# Revit family: 0053546 Feilo Sylvania Lighting Fixture START SPOT LED IP65 4000K G2
name_source: partatom
category: Lighting Fixtures
revit_build: Autodesk Revit 2017 (Build: 20190507_1515(x64)
units: mm (PartAtom-declared; Revit-internal decimal feet)

## family parameters
Cut with Voids When Loaded = No
Host = Face
Light Source = Yes
OmniClass Number = 23.80.70.00
OmniClass Title = Lighting
Part Type = Normal
Room Calculation Point = No
Round Connector Dimension = Use Diameter
Shared = No

## types (1)
- 0053546 START SPOT LED IP65 4000K G2
    Apparent Load = 7 VA
    Assembly Code = D5020200
    AssetType = Fixed
    ClassificationName = Uniclass2015
    ClassificationValue = EF_70_80
    Color Filter = 16777215
    Cost = 0 $
    Default Elevation = 1219 mm
    DepthDiffuser_FEILO = 3 mm  [stored 0.00984252 ft]
    Description = Integrated LED IP65 fixed downlight, RAL9016, 525LM, 6.5W, 4000K, 100 degree beam angle, polycarbonate white body, low profile 58mm recessed depth, 86mm bezel diameter, 68-74mm cutout, frosted lens.
    DiameterBezel_FEILO = 86 mm  [stored 0.282152 ft]
    Dimming Lamp Color Temperature Shift = <None>
    DocumentationLiterature = http://www.sylvania-lighting.com
    DurationUnit = hours
    ElectricShockClassification = Class II
    Emit Shape Visible in Rendering = No
    Emit from Circle Diameter = 38 mm  [stored 0.124672 ft]
    ExpectedLife = 50000
    HeightBezel_FEILO = 2 mm  [stored 0.00656168 ft]
    IfcExportAs = IfcLightFixtureType
    IfcExportType = IfcLightFixtureType
    ImpactProtectionIndex = IK03
    IngressProtection = IP65
    InputNominalFrequency = 50/60 Hz
    InputVoltage = 220-240V~
    Keynote = 16500
    Lamp = LED
    LampColourRenderingIndex = 80
    LampColourTemperature = 4000 K
    LampNominalLuminous = 525 lm
    LampsType = LED
    LightOutputRatio = 100
    LuminousEfficacy = 81 lm/W
    Manufacturer = Feilo Sylvania
    ManufacturerName = Feilo Sylvania
    Material = polycarbonate housing, acrylic diffuser
    Material_1_FEILO = Body-Sylvania-StartSpot-White
    Material_2_FEILO = LED-Sylvania-StartSpot
    Material_3_FEILO = <By Category>
    Material_4_FEILO = <By Category>
    Model = START SPOT LED IP65 4000K G2
    ModelNumber = 0053546
    ModelReference = START SPOT LED IP65 4000K G2
    Name = START SPOT LED IP65 4000K G2
    NominalDepth = 86 mm  [stored 0.282152 ft]
    NominalHeight = 60 mm
    NominalLength = 86 mm  [stored 0.282152 ft]
    Photometric Web File = 0053546.ies
    PowerConsumption = 7 W
    PowerFactor = 0
    RadiusCutout_FEILO = 36 mm
    RadiusDiffuser_FEILO = 19 mm
    RadiusOptics_FEILO = 99 mm
    Tilt Angle = -90.00°
    Type Image = <None>
    TypeName = START SPOT LED IP65 4000K G2
    URL = http://www.sylvania-lighting.com
    VisibilityTop_FEILO = Yes
    Voltage = 230 V
    Weight = 3.648 kg

note: [stored X ft] marks values corroborated as IEEE doubles in the binary element streams (Revit-internal decimal feet)

## geometry (parser evidence)
native form markers: Sweep x3
no freeform markers — native parametric forms only
